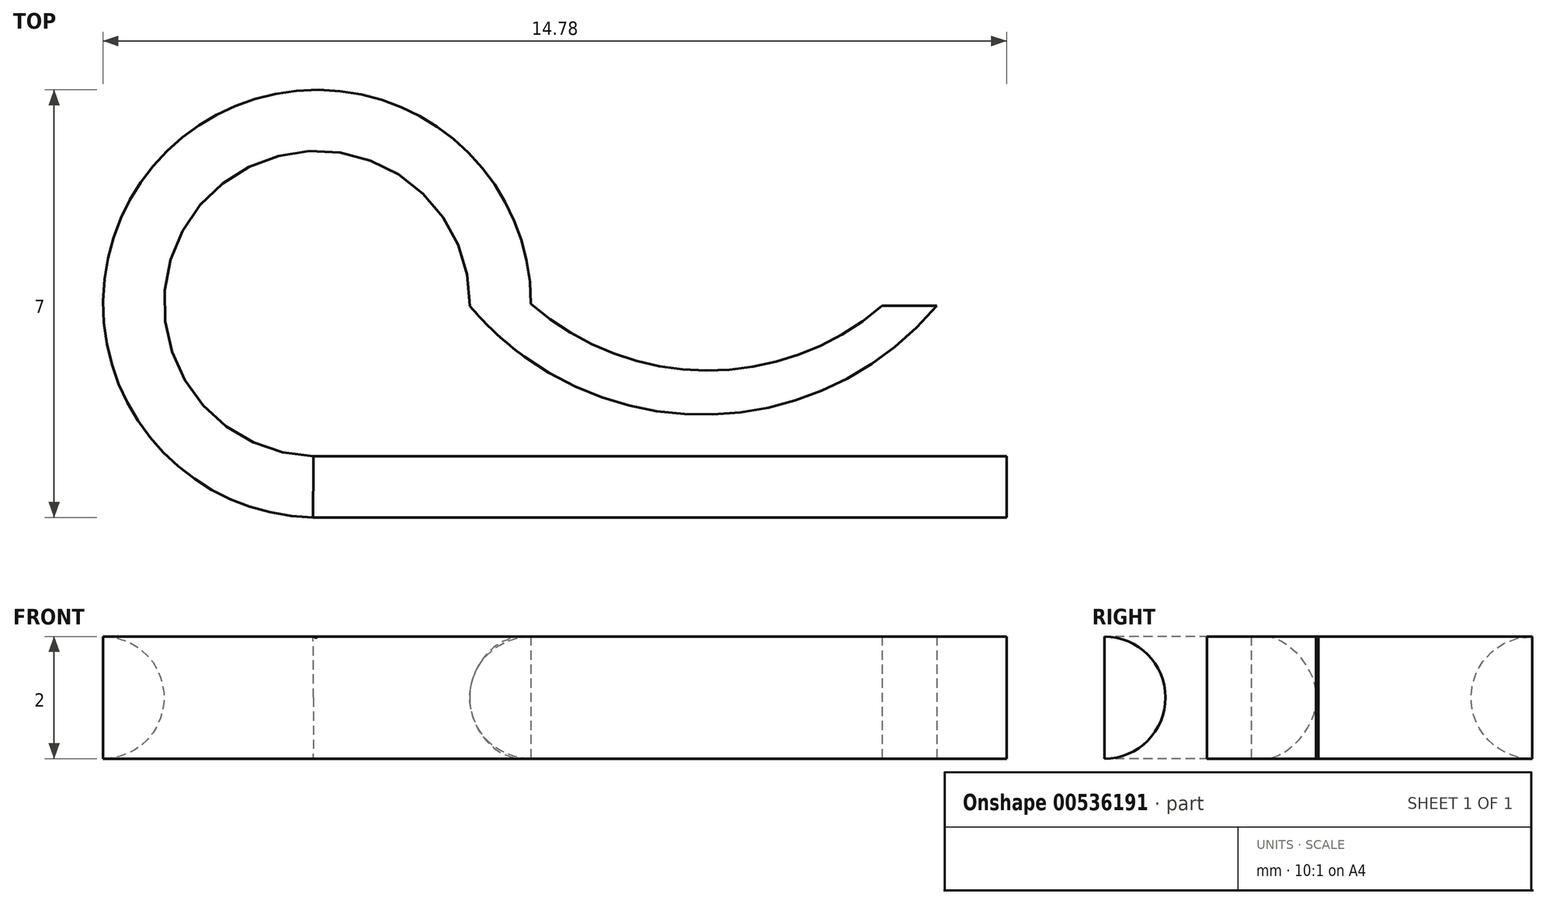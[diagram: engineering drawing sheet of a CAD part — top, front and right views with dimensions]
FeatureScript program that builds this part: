
annotation { "Feature Type Name" : "Feature", "Feature Type Description" : "" }
export const myFeature = defineFeature(function(context is Context, id is Id, definition is map)
    precondition{}
    {
        {
            var Q0;
            Q0=qCreatedBy(makeId("Top.planeOp"),FACE);
            var sketch = newSketch(context, id + "F0", { "sketchPlane" : qUnion([Q0])});
            skArc(sketch, "E0", {"start": v(3.5, 0) * mm, "mid": v(-2.47, 2.48) * mm, "end": v(-0.01, -3.5) * mm});
            skArc(sketch, "E1", {"start": v(2.5, -0.04) * mm, "mid": v(-1.74, 1.8) * mm, "end": v(-0.06, -2.5) * mm});
            skLineSegment(sketch, "E2.bottom", {"start": v(-0.06, -2.5) * mm, "end": v(11.28, -2.5) * mm});
            skLineSegment(sketch, "E2.top", {"start": v(-0.06, -3.5) * mm, "end": v(11.28, -3.5) * mm});
            skLineSegment(sketch, "E2.right", {"start": v(11.28, -2.5) * mm, "end": v(11.28, -3.5) * mm});
            skArc(sketch, "E3", {"start": v(2.5, -0.04) * mm, "mid": v(6.32, -1.82) * mm, "end": v(10.14, -0.04) * mm});
            skArc(sketch, "E4", {"start": v(3.5, 0) * mm, "mid": v(6.37, -1.1) * mm, "end": v(9.24, -0.04) * mm});
            skLineSegment(sketch, "E5", {"start": v(9.24, -0.04) * mm, "end": v(10.14, -0.04) * mm});
            skSolve(sketch);
        }
        {
            var Q0;
            Q0 = qSketchRegion(id + "F0", true);
            extrude(context, id + "F1", {"entities" : qUnion([Q0]), "depth" : 2 * mm, "offsetDistance" : 25 * mm});
        }
        {
            var Q0;
            Q0=makeQuery(id+"F1.opExtrude","CAP_EDGE",EDGE,{"disambiguationData":[OSD([sQuery(id+"F0.wireOp",EDGE,"E2.bottom")])],"isStart":true});
            var Q1;
            Q1=makeQuery(id+"F1.opExtrude","CAP_EDGE",EDGE,{"disambiguationData":[OSD([sQuery(id+"F0.wireOp",EDGE,"E2.bottom")])],"isStart":false});
            fillet(context, id + "F2", {"entities" : qUnion([Q0, Q1]), "radius" : 1 * mm, "tangentPropagation" : true, "allowEdgeOverflow" : false});
        }
        {
            var Q0;
            Q0=makeQuery(id+"F1.opExtrude","CAP_EDGE",EDGE,{"disambiguationData":[OSD([sQuery(id+"F0.wireOp",EDGE,"E2.top")])],"isStart":false});
            fillet(context, id + "F3", {"entities" : qUnion([Q0]), "radius" : 1 * mm, "tangentPropagation" : true, "allowEdgeOverflow" : false});
        }
    });
